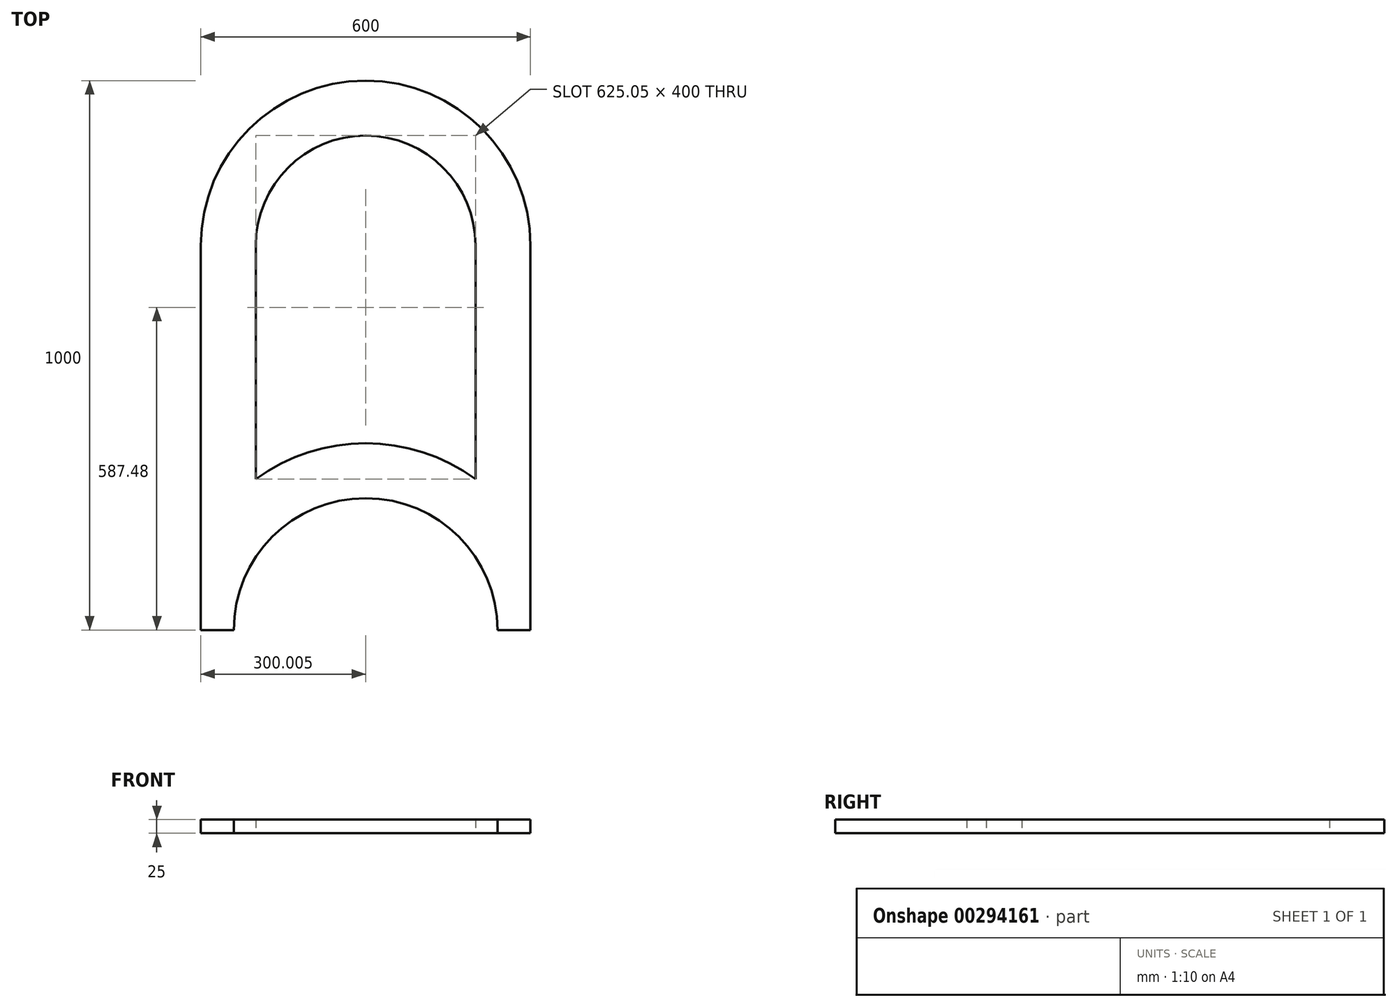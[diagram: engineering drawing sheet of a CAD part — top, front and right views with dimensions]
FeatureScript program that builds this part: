
annotation { "Feature Type Name" : "Feature", "Feature Type Description" : "" }
export const myFeature = defineFeature(function(context is Context, id is Id, definition is map)
    precondition{}
    {
        {
            var Q0;
            Q0=qCreatedBy(makeId("Top.planeOp"),FACE);
            var sketch = newSketch(context, id + "F0", { "sketchPlane" : qUnion([Q0])});
            skLineSegment(sketch, "E0", {"start": v(-331.95, 506.1) * mm, "end": v(-331.95, -193.9) * mm});
            skLineSegment(sketch, "E1", {"start": v(268.05, 506.1) * mm, "end": v(268.05, -193.9) * mm});
            skLineSegment(sketch, "E2", {"start": v(-331.95, -193.9) * mm, "end": v(-271.95, -193.9) * mm});
            skLineSegment(sketch, "E3", {"start": v(-31.95, 806.1) * mm, "end": v(-31.95, 806.1) * mm});
            skLineSegment(sketch, "E4", {"start": v(208.05, -193.9) * mm, "end": v(268.05, -193.9) * mm});
            skArc(sketch, "E5", {"start": v(208.05, -193.9) * mm, "mid": v(-31.95, 46.1) * mm, "end": v(-271.95, -193.9) * mm});
            skPoint(sketch, "E6.visualSharp", {"position": v(-331.95, 806.1) * mm});
            skArc(sketch, "E6.filletArc", {"start": v(-31.95, 806.1) * mm, "mid": v(-244.08, 718.23) * mm, "end": v(-331.95, 506.1) * mm});
            skPoint(sketch, "E7.visualSharp", {"position": v(268.05, 806.1) * mm});
            skArc(sketch, "E7.filletArc", {"start": v(268.05, 506.1) * mm, "mid": v(180.19, 718.23) * mm, "end": v(-31.95, 806.1) * mm});
            skArc(sketch, "E8", {"start": v(168.05, 506.1) * mm, "mid": v(-31.95, 706.1) * mm, "end": v(-231.95, 506.1) * mm});
            skLineSegment(sketch, "E9", {"start": v(-231.95, 81.06) * mm, "end": v(-231.95, 542.76) * mm});
            skLineSegment(sketch, "E10", {"start": v(168.05, 506.1) * mm, "end": v(168.05, 81.06) * mm});
            skArc(sketch, "E11.trimOffspring", {"start": v(168.05, 81.06) * mm, "mid": v(-31.95, 146.1) * mm, "end": v(-231.95, 81.06) * mm});
            skSolve(sketch);
        }
        {
            var Q0;
            Q0 = qSketchRegion(id + "F0", true);
            extrude(context, id + "F1", {"entities" : qUnion([Q0]), "depth" : 25 * mm});
        }
    });
